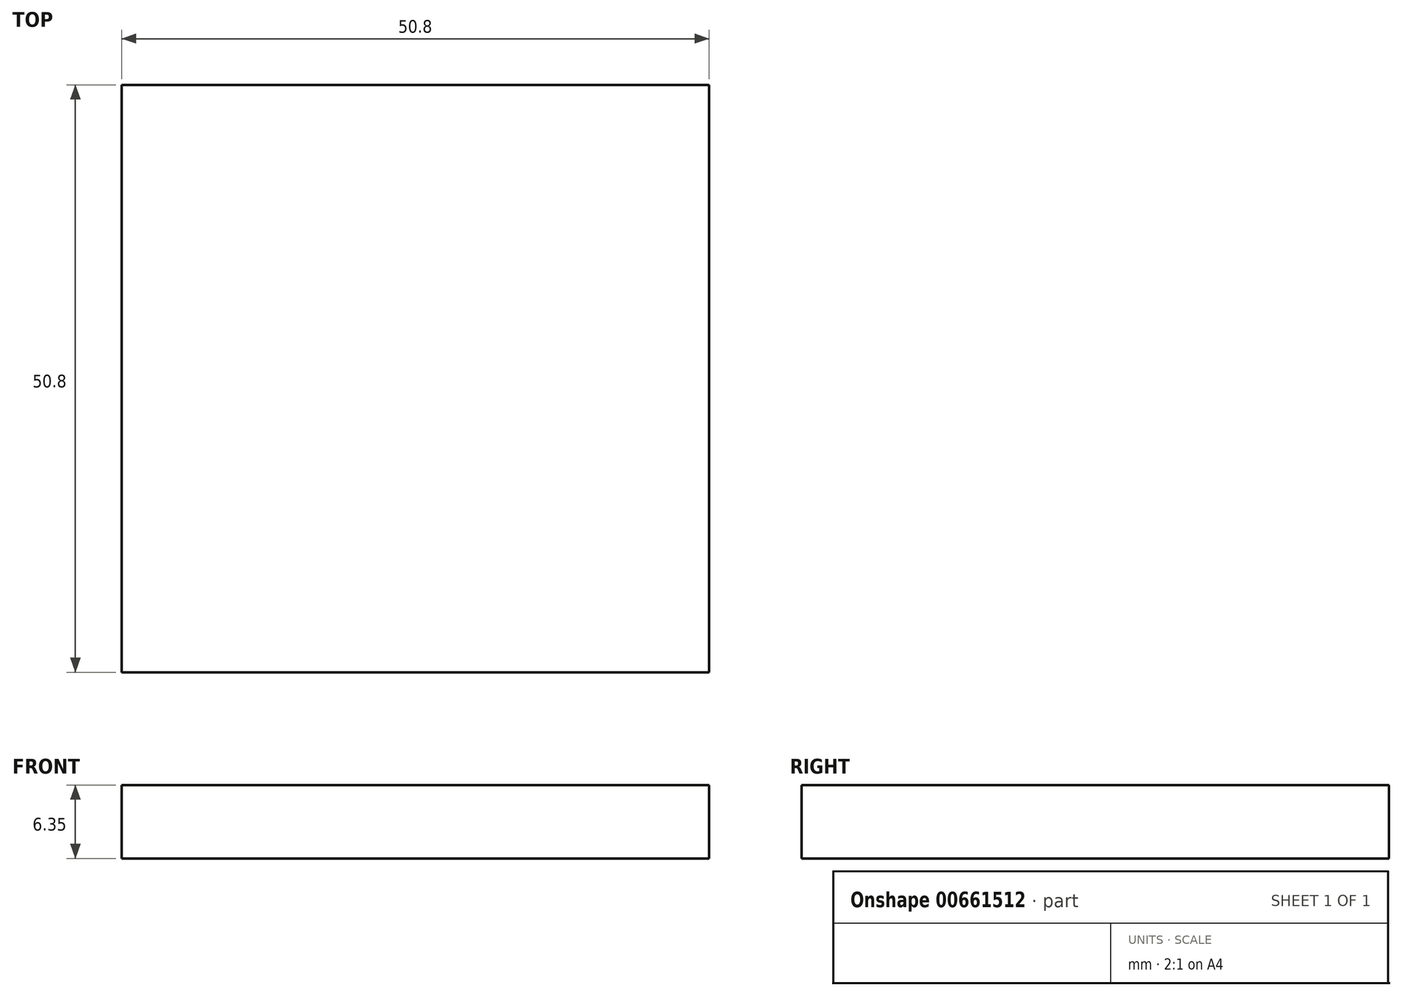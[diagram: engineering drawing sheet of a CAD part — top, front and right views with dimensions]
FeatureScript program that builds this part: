
annotation { "Feature Type Name" : "Feature", "Feature Type Description" : "" }
export const myFeature = defineFeature(function(context is Context, id is Id, definition is map)
    precondition{}
    {
        {
            var Q0;
            Q0=qCreatedBy(makeId("Top.planeOp"),FACE);
            var sketch = newSketch(context, id + "F0", { "sketchPlane" : qUnion([Q0])});
            skLineSegment(sketch, "E0.bottom", {"start": v(0, 0) * mm, "end": v(-50.8, 0) * mm});
            skLineSegment(sketch, "E0.top", {"start": v(0, 50.8) * mm, "end": v(-50.8, 50.8) * mm});
            skLineSegment(sketch, "E0.left", {"start": v(0, 0) * mm, "end": v(0, 50.8) * mm});
            skLineSegment(sketch, "E0.right", {"start": v(-50.8, 0) * mm, "end": v(-50.8, 50.8) * mm});
            skSolve(sketch);
        }
        {
            var Q0;
            Q0=makeQuery(id+"F0.imprint","IMPRINT",FACE,{"disambiguationData":[TD([[makeQuery(id+"F0.imprint","IMPRINT",EDGE,{"derivedFrom":sQuery(id+"F0.wireOp",EDGE,"E0.bottom")}),-1.0]])]});
            extrude(context, id + "F1", {"entities" : qUnion([Q0]), "depth" : 6.35 * mm, "offsetDistance" : 25.4 * mm});
        }
    });
